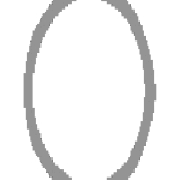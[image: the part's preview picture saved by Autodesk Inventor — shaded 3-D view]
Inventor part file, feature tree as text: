
AUTODESK INVENTOR PART (.ipt)
format: ipt  version: 2021 (Build 250183000, 183)  size: 128,512 bytes
history: native  units: in
note: dims shown in document units (in); Inventor stores cm internally (conversion verified against a paired STEP export)
features: other x4, plane x4, sketch x4, extrude x1, boolean_combine x1
ambient origin geometry x8: Origin, YZ Plane, XZ Plane, XY Plane, X Axis, Y Axis, Z Axis, Center Point
bodies: Solid1 (feature_tree), Body (feature_tree), Solid2 (feature_tree)
feature tree (14):
  other  "Driven Length"
  other  "Frame Generator"
  other  "Start Plane"
  other  "End Plane"
  plane  "Work Plane4"
  plane  "Work Plane5"
  plane  "Work Plane6"
  extrude  "Extrusion3"  Depth=0.065in
  boolean_combine  "Combine1"
  sketch  "Sketch"  dims[d5=6.7082in d6=0.12in d7=0.0in d8=90.0deg d9=6.7082in d10=0.12in d11=0.0in]
  sketch  "Sketch2"  dims[d0=1.0in d1=0.065in]
  plane  "Work Plane3"
  sketch  "Sketch3"  dims[d2=6.7082in]
  sketch  "Sketch4"  dims[d4=-0.0in]
